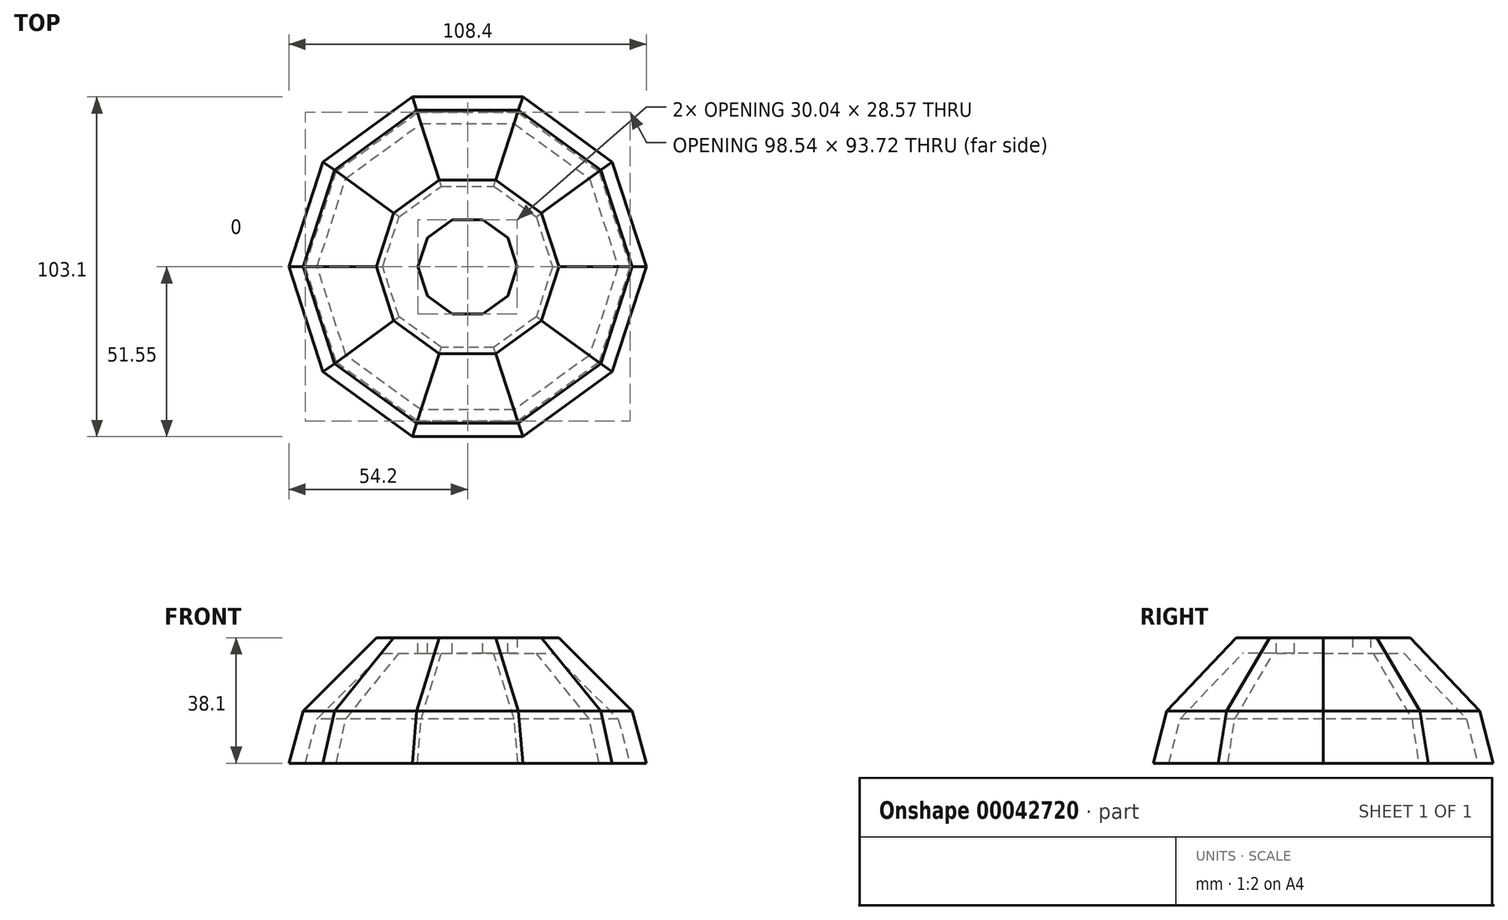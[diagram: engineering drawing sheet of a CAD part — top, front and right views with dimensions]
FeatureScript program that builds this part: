
annotation { "Feature Type Name" : "Feature", "Feature Type Description" : "" }
export const myFeature = defineFeature(function(context is Context, id is Id, definition is map)
    precondition{}
    {
        {
            var Q0;
            Q0=qCreatedBy(makeId("Top.planeOp"),FACE);
            var sketch = newSketch(context, id + "F0", { "sketchPlane" : qUnion([Q0])});
            skCircle(sketch, "E0.cCircle", {"center": v(0, 0) * mm, "radius": 51.55 * mm, "construction": true});
            skLineSegment(sketch, "E0.0", {"start": v(-16.75, 51.55) * mm, "end": v(16.75, 51.55) * mm});
            skLineSegment(sketch, "E0.1", {"start": v(16.75, 51.55) * mm, "end": v(43.85, 31.86) * mm});
            skLineSegment(sketch, "E0.2", {"start": v(43.85, 31.86) * mm, "end": v(54.2, 0) * mm});
            skLineSegment(sketch, "E0.3", {"start": v(54.2, 0) * mm, "end": v(43.85, -31.86) * mm});
            skLineSegment(sketch, "E0.4", {"start": v(43.85, -31.86) * mm, "end": v(16.75, -51.55) * mm});
            skLineSegment(sketch, "E0.5", {"start": v(16.75, -51.55) * mm, "end": v(-16.75, -51.55) * mm});
            skLineSegment(sketch, "E0.6", {"start": v(-16.75, -51.55) * mm, "end": v(-43.85, -31.86) * mm});
            skLineSegment(sketch, "E0.7", {"start": v(-43.85, -31.86) * mm, "end": v(-54.2, 0) * mm});
            skLineSegment(sketch, "E0.8", {"start": v(-54.2, 0) * mm, "end": v(-43.85, 31.86) * mm});
            skLineSegment(sketch, "E0.9", {"start": v(-43.85, 31.86) * mm, "end": v(-16.75, 51.55) * mm});
            skPoint(sketch, "E0.0.midPoint", {"position": v(0, 51.55) * mm});
            skSolve(sketch);
        }
        {
            var Q0;
            Q0=qCreatedBy(makeId("Front.planeOp"),FACE);
            var sketch = newSketch(context, id + "F1", { "sketchPlane" : qUnion([Q0])});
            skLineSegment(sketch, "E1", {"start": v(0, 0) * mm, "end": v(0, 38.1) * mm});
            skLineSegment(sketch, "E2", {"start": v(0, 38.1) * mm, "end": v(27.72, 38.1) * mm});
            skLineSegment(sketch, "E3", {"start": v(27.72, 38.1) * mm, "end": v(49.95, 15.88) * mm});
            skPoint(sketch, "E4.0", {"position": v(54.2, 0) * mm});
            skLineSegment(sketch, "E5", {"start": v(49.95, 15.87) * mm, "end": v(54.2, 0) * mm});
            skLineSegment(sketch, "E6.0", {"start": v(0, 0) * mm, "end": v(49.27, 0) * mm});
            skLineSegment(sketch, "E7.0", {"start": v(45.68, 13.4) * mm, "end": v(49.6, -1.23) * mm});
            skLineSegment(sketch, "E7.1", {"start": v(25.75, 33.34) * mm, "end": v(45.68, 13.4) * mm});
            skLineSegment(sketch, "E7.2", {"start": v(0, 33.34) * mm, "end": v(25.75, 33.34) * mm});
            skLineSegment(sketch, "E8", {"start": v(15.02, 38.1) * mm, "end": v(15.02, 33.34) * mm});
            skLineSegment(sketch, "E9", {"start": v(54.2, 0) * mm, "end": v(49.27, 0) * mm});
            skSolve(sketch);
        }
        {
            var Q0;
            {var subQ3=sQuery(id+"F1.wireOp",EDGE,"E3");Q0=makeQuery(id+"F1.imprint","IMPRINT",FACE,{"disambiguationData":[TD([[makeQuery(id+"F1.imprint","IMPRINT",EDGE,{"derivedFrom":subQ3}),-1.0]])]});}
            var Q1;
            Q1=sQuery(id+"F0.wireOp",EDGE,"E0.2");
            var Q2;
            Q2=sQuery(id+"F0.wireOp",EDGE,"E0.1");
            var Q3;
            Q3=sQuery(id+"F0.wireOp",EDGE,"E0.0");
            var Q4;
            Q4=sQuery(id+"F0.wireOp",EDGE,"E0.9");
            var Q5;
            Q5=sQuery(id+"F0.wireOp",EDGE,"E0.8");
            var Q6;
            Q6=sQuery(id+"F0.wireOp",EDGE,"E0.7");
            var Q7;
            Q7=sQuery(id+"F0.wireOp",EDGE,"E0.6");
            var Q8;
            Q8=sQuery(id+"F0.wireOp",EDGE,"E0.5");
            var Q9;
            Q9=sQuery(id+"F0.wireOp",EDGE,"E0.4");
            var Q10;
            Q10=sQuery(id+"F0.wireOp",EDGE,"E0.3");
            sweep(context, id + "F2", {"profiles" : qUnion([Q0]), "path" : qUnion([Q1, Q2, Q3, Q4, Q5, Q6, Q7, Q8, Q9, Q10])});
        }
    });
